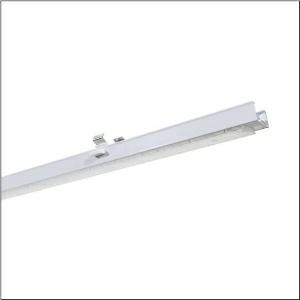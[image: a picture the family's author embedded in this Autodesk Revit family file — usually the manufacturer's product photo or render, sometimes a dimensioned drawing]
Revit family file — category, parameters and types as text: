
# Revit family: trunking_flex_31_51re12mb58b
name_source: partatom
category: Lighting Fixtures
units: mm (PartAtom-declared; Revit-internal decimal feet)

## family parameters
Cut with Voids When Loaded = No
Host = Face
Light Source = No
Part Type = Normal
Room Calculation Point = No
Round Connector Dimension = Use Diameter
Shared = No

## types (1)
- --- (1 x LED, 8000 lm, 50 W, 5000K)
    Apparent Load = 50 VA
    CIE Flux Codes = 65 91 98 99 100
    Color Rendering = 80
    Color Temperature = 5000K
    Default Elevation = 1800 mm
    Description = Trunking Flex 31, luminaire insert, of extruded aluminium section, coated, traffic white (RAL 9016), length: 1.472mm, width: 91mm, height: 53mm, LED rated luminous flux: 8.000lm, light colour: 850, control gear: ON/OFF Multilumen, with system connector: socket, mains connection: 220..240V, AC, 50/60Hz, rated input power: 50W, luminous flux adjustable on luminaire in four steps (4130/5610/6850/8000lm), connected load according to luminous flux setting (25/34/42/50W), primary light control with lens, of plastic, primary optical cover: cover, of PMMA, light emission: direct distribution, protection rating (complete): IP20, insulation class (complete): insulation class I (protective earthing), certification: CE, UKCA, impact resistance: IK02, permissible ambient temperature for indoor applications: -20..+40°C, packaging unit: 1 piece
    Height = 58 mm
    Lamp = 1 x LED
    Lamp Light Flux = 8000 lm
    Lamp Power = 50 W
    Lamp count = 1
    Length = 1472 mm
    Luminous efficacy = 160 lm/W
    Manufacturer = Siteco
    ModVariant = No
    Model = 51RE12MB58B
    Mounting Place = Ceiling
    Mounting Type = Pendant
    Number of Poles = 1
    OnlyDefault = Yes
    Power Factor = 1
    Product Name = Trunking Flex 31
    Product group = luminaire insert | ceiling pendant
    ProductGroupID = 902
    Protection Class = Protection class I
    Protection Degree = IP 20
    RLX_Detail_Level = 1
    RLX_Emergency_Light_Flux = 0 lm
    RLX_Emergency_Type = 0
    RLX_Emergency_Type_DB = No
    RlxData = <blob elided: 20369 chars, md5=7da0da46>
    Socket = socket
    Standby Power = 0 W
    System Light Flux = 8000 lm
    System Power = 50 W
    Type Comments = factory setting: luminous flux: 100 % | (ON | ON) | 300 mA
    Type Image = l_1266702.jpg
    URL = http://relux.com
    VarID = @adj_079227
    Voltage = 0 V
    Weight = 0.00 kg
    Width = 65 mm

## geometry (parser evidence)
native form markers: Blend x4, Sweep x13
no freeform markers — native parametric forms only
